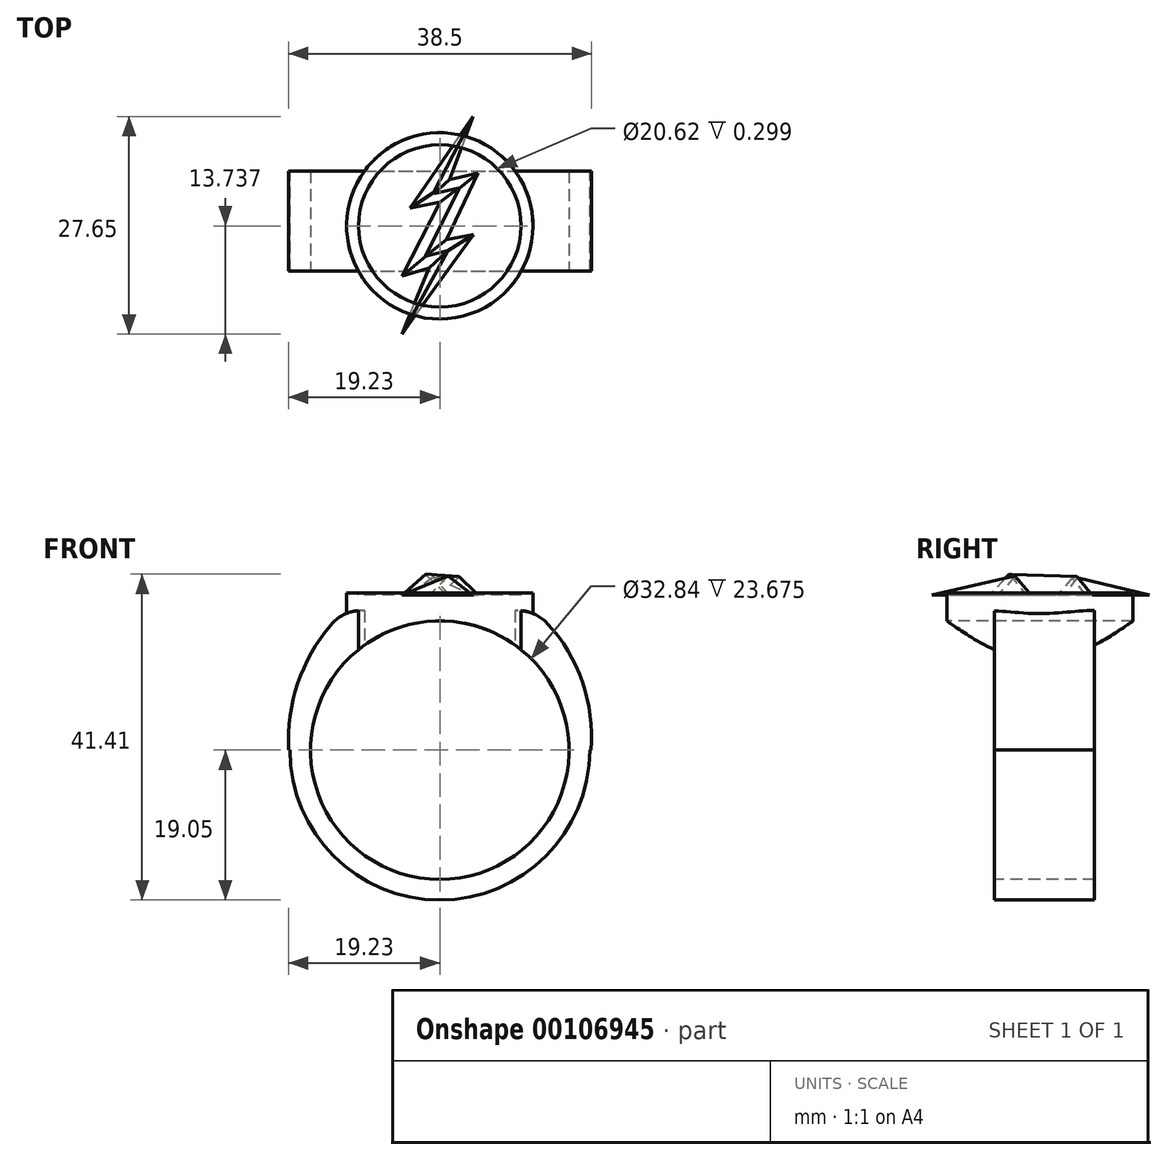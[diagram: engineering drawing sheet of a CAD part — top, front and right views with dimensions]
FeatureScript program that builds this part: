
annotation { "Feature Type Name" : "Feature", "Feature Type Description" : "" }
export const myFeature = defineFeature(function(context is Context, id is Id, definition is map)
    precondition{}
    {
        {
            var Q0;
            Q0=qCreatedBy(makeId("Front.planeOp"),FACE);
            var sketch = newSketch(context, id + "F0", { "sketchPlane" : qUnion([Q0])});
            skCircle(sketch, "E0", {"center": v(0, 0) * mm, "radius": 19.05 * mm});
            skSolve(sketch);
        }
        {
            var Q0;
            Q0=makeQuery(id+"F0.imprint","IMPRINT",FACE,{"disambiguationData":[TD([[makeQuery(id+"F0.imprint","IMPRINT",EDGE,{"derivedFrom":sQuery(id+"F0.wireOp",EDGE,"E0")}),1.0]])]});
            extrude(context, id + "F1", {"entities" : qUnion([Q0]), "depth" : 12.7 * mm});
        }
        {
            var Q0;
            Q0=makeQuery(id+"F1.opExtrude","CAP_FACE",FACE,{"disambiguationData":[OSD([sQuery(id+"F0.wireOp",EDGE,"E0")])],"isStart":false});
            var sketch = newSketch(context, id + "F2", { "sketchPlane" : qUnion([Q0])});
            skCircle(sketch, "E1", {"center": v(0, 0) * mm, "radius": 16.42 * mm});
            skSolve(sketch);
        }
        {
            var Q0;
            Q0=makeQuery(id+"F2.imprint","IMPRINT",FACE,{"disambiguationData":[TD([[makeQuery(id+"F2.imprint","IMPRINT",EDGE,{"derivedFrom":sQuery(id+"F2.wireOp",EDGE,"E1")}),1.0]])]});
            extrude(context, id + "F3", {"entities" : qUnion([Q0]), "operationType" : NewBodyOperationType.REMOVE, "oppositeDirection" : true, "depth" : 12.7 * mm});
        }
        {
            var Q0;
            Q0=qCreatedBy(makeId("Top.planeOp"),FACE);
            var sketch = newSketch(context, id + "F4", { "sketchPlane" : qUnion([Q0])});
            skCircle(sketch, "E2", {"center": v(0, -6.95) * mm, "radius": 11.83 * mm});
            skSolve(sketch);
        }
        {
            var Q0;
            Q0 = qSketchRegion(id + "F4", true);
            extrude(context, id + "F5", {"entities" : qUnion([Q0]), "operationType" : NewBodyOperationType.ADD, "depth" : 20 * mm});
        }
        {
            var Q0;
            Q0=makeQuery(id+"F2.imprint","IMPRINT",FACE,{"disambiguationData":[TD([[makeQuery(id+"F2.imprint","IMPRINT",EDGE,{"derivedFrom":sQuery(id+"F2.wireOp",EDGE,"E1")}),1.0]])]});
            extrude(context, id + "F6", {"entities" : qUnion([Q0]), "operationType" : NewBodyOperationType.REMOVE, "depth" : 6.22 * mm});
        }
        {
            var Q0;
            Q0=makeQuery(id+"F2.imprint","IMPRINT",FACE,{"disambiguationData":[TD([[makeQuery(id+"F2.imprint","IMPRINT",EDGE,{"derivedFrom":sQuery(id+"F2.wireOp",EDGE,"E1")}),1.0]])]});
            extrude(context, id + "F7", {"entities" : qUnion([Q0]), "operationType" : NewBodyOperationType.REMOVE, "oppositeDirection" : true, "depth" : 19.74 * mm});
        }
        {
            var Q0;
            Q0=qCreatedBy(makeId("Front.planeOp"),FACE);
            var sketch = newSketch(context, id + "F8", { "sketchPlane" : qUnion([Q0])});
            skLineSegment(sketch, "E3", {"start": v(-12.14, 17.73) * mm, "end": v(11.95, 17.73) * mm});
            skLineSegment(sketch, "E4", {"start": v(-19.2, 0) * mm, "end": v(19.2, 0) * mm});
            skArc(sketch, "E5", {"start": v(19.2, 0) * mm, "mid": v(17.7, 9.74) * mm, "end": v(11.95, 17.73) * mm});
            skArc(sketch, "E6", {"start": v(-12.14, 17.73) * mm, "mid": v(-17.6, 9.63) * mm, "end": v(-19.2, 0) * mm});
            skSolve(sketch);
        }
        {
            var Q0;
            Q0=makeQuery(id+"F8.imprint","IMPRINT",FACE,{"disambiguationData":[TD([[makeQuery(id+"F8.imprint","IMPRINT",EDGE,{"derivedFrom":sQuery(id+"F8.wireOp",EDGE,"E3")}),-1.0]])]});
            var Q1;
            Q1=sQuery(id+"F8.wireOp",EDGE,"E5");
            var Q2;
            Q2=sQuery(id+"F8.wireOp",EDGE,"E6");
            extrude(context, id + "F9", {"entities" : qUnion([Q0]), "operationType" : NewBodyOperationType.ADD, "surfaceEntities" : qUnion([Q1, Q2]), "depth" : 12.7 * mm});
        }
        {
            var Q0;
            Q0=makeQuery(id+"F2.imprint","IMPRINT",FACE,{"disambiguationData":[TD([[makeQuery(id+"F2.imprint","IMPRINT",EDGE,{"derivedFrom":sQuery(id+"F2.wireOp",EDGE,"E1")}),1.0]])]});
            extrude(context, id + "F10", {"entities" : qUnion([Q0]), "operationType" : NewBodyOperationType.REMOVE, "oppositeDirection" : true, "depth" : 25.4 * mm});
        }
        {
            var Q0;
            Q0=makeQuery(id+"F9.opExtrude","SWEPT_EDGE",EDGE,{"disambiguationData":[OSD([sQuery(id+"F8.wireOp",EDGE,"E3"),sQuery(id+"F8.wireOp",EDGE,"E5")])]});
            var Q1;
            Q1=makeQuery(id+"F9.opExtrude","SWEPT_EDGE",EDGE,{"disambiguationData":[OSD([sQuery(id+"F8.wireOp",EDGE,"E3"),sQuery(id+"F8.wireOp",EDGE,"E6")])]});
            fillet(context, id + "F11", {"entities" : qUnion([Q0, Q1]), "radius" : 5.08 * mm, "tangentPropagation" : true, "allowEdgeOverflow" : false});
        }
        {
            var Q0;
            Q0=makeQuery(id+"F5.opExtrude","CAP_FACE",FACE,{"disambiguationData":[OSD([sQuery(id+"F4.wireOp",EDGE,"E2")])],"isStart":false});
            var sketch = newSketch(context, id + "F12", { "sketchPlane" : qUnion([Q0])});
            skCircle(sketch, "E7", {"center": v(0, -6.95) * mm, "radius": 10.3 * mm});
            skSolve(sketch);
        }
        {
            var Q0;
            Q0=makeQuery(id+"F12.imprint","IMPRINT",FACE,{"disambiguationData":[TD([[makeQuery(id+"F12.imprint","IMPRINT",EDGE,{"derivedFrom":sQuery(id+"F12.wireOp",EDGE,"E7")}),1.0]])]});
            var Q1;
            Q1=sQuery(id+"F12.wireOp",EDGE,"E7");
            extrude(context, id + "F13", {"entities" : qUnion([Q0]), "operationType" : NewBodyOperationType.REMOVE, "surfaceEntities" : qUnion([Q1]), "oppositeDirection" : true, "depth" : 0.3 * mm});
        }
        {
            var Q0;
            Q0=makeQuery(id+"F13.boolean.opBoolean","COPY",FACE,{"derivedFrom":makeQuery(id+"F13.opExtrude","CAP_FACE",FACE,{"disambiguationData":[OSD([sQuery(id+"F12.wireOp",EDGE,"E7")])],"isStart":false})});
            var sketch = newSketch(context, id + "F14", { "sketchPlane" : qUnion([Q0])});
            skLineSegment(sketch, "E8", {"start": v(-3.79, -4.7) * mm, "end": v(0, -3.96) * mm});
            skLineSegment(sketch, "E9", {"start": v(-4.8, -13.33) * mm, "end": v(-1.34, -12.28) * mm});
            skLineSegment(sketch, "E10", {"start": v(0.87, -8.71) * mm, "end": v(4.26, -8.05) * mm});
            skLineSegment(sketch, "E11", {"start": v(1.23, -1.09) * mm, "end": v(4.88, -0.27) * mm});
            skLineSegment(sketch, "E12", {"start": v(0, -3.96) * mm, "end": v(-4.8, -13.33) * mm});
            skLineSegment(sketch, "E13", {"start": v(-1.34, -12.28) * mm, "end": v(-4.8, -20.69) * mm});
            skLineSegment(sketch, "E14", {"start": v(-4.8, -20.69) * mm, "end": v(4.26, -8.05) * mm});
            skLineSegment(sketch, "E15", {"start": v(4.88, -0.27) * mm, "end": v(0.87, -8.71) * mm});
            skLineSegment(sketch, "E16", {"start": v(1.23, -1.09) * mm, "end": v(4.22, 6.96) * mm});
            skLineSegment(sketch, "E17", {"start": v(4.22, 6.96) * mm, "end": v(-3.79, -4.7) * mm});
            skLineSegment(sketch, "E18", {"start": v(-2.04, -11.23) * mm, "end": v(1.04, -10.3) * mm});
            skLineSegment(sketch, "E19", {"start": v(1.04, -10.3) * mm, "end": v(4.26, -8.05) * mm});
            skLineSegment(sketch, "E20", {"start": v(2.2, -1.56) * mm, "end": v(-2.04, -11.23) * mm});
            skLineSegment(sketch, "E21", {"start": v(-2.04, -11.23) * mm, "end": v(-4.8, -13.33) * mm});
            skLineSegment(sketch, "E22", {"start": v(1.04, -10.3) * mm, "end": v(-4.8, -20.69) * mm});
            skLineSegment(sketch, "E23", {"start": v(-1.34, -12.28) * mm, "end": v(1.04, -10.3) * mm});
            skLineSegment(sketch, "E24", {"start": v(-2.04, -11.23) * mm, "end": v(0.87, -8.71) * mm});
            skSolve(sketch);
        }
        {
            var Q0;
            Q0 = qSketchRegion(id + "F14", true);
            extrude(context, id + "F15", {"entities" : qUnion([Q0]), "depth" : 4.64 * mm, "hasDraft" : true, "draftAngle" : 30 * degree, "draftPullDirection" : true});
        }
    });
